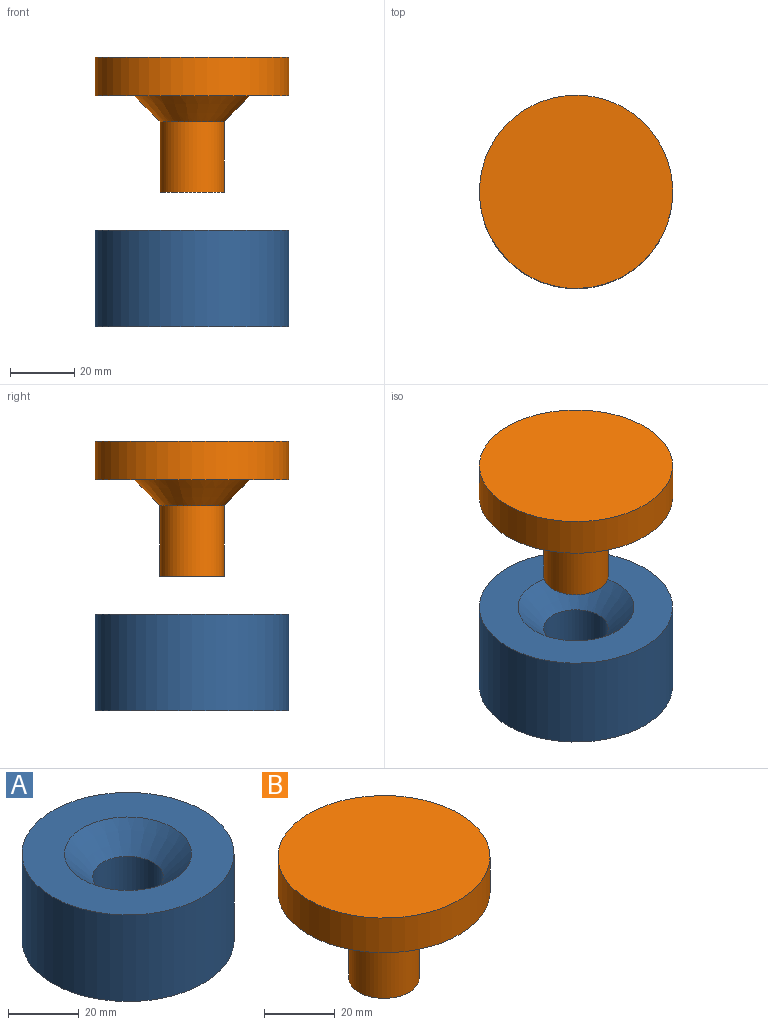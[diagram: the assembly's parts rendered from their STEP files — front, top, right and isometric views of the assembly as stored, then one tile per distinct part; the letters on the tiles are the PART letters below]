
ASSEMBLY  parts=2 mates=1
PART A: 5 faces, bbox 60x60x30 mm
  f0: plane 60x60mm, normal (0,0,-1), area 2513.3mm2, adj f1,f4
  f1: cylinder r=10mm len=22mm, axis (0,0,-1), area 1382.3mm2, adj f0,f2
  f2: cone r=10mm half-angle=45deg, axis (0,0,1), area 995.2mm2, adj f1,f3
  f3: plane 60x60mm, normal (0,0,1), area 1809.6mm2, adj f2,f4
  f4: cylinder r=30mm len=60mm, axis (0,0,-1), area 5654.9mm2, adj f0,f3
PART B: 6 faces, bbox 60x60x42 mm
  f0: plane 60x60mm, normal (0,0,1), area 2827.4mm2, adj f1
  f1: cylinder r=30mm len=60mm, axis (0,0,-1), area 2261.9mm2, adj f0,f2
  f2: plane 60x60mm, normal (0,0,-1), area 1809.6mm2, adj f1,f3
  f3: cone r=9.95mm half-angle=45deg, axis (0,0,1), area 999.6mm2, adj f2,f4
  f4: cylinder r=9.95mm len=21.95mm, axis (0,0,-1), area 1372.3mm2, adj f3,f5
  f5: plane 19.9x19.9mm, normal (0,0,-1), area 311mm2, adj f4
PLACE A t=(-0.84,-7.45,-4.56)mm
PLACE B t=(-0.84,-7.45,37.23)mm
MATE cylindrical B.f1 <-> A.f1  axis (0,0,-1) through (-0.84,-7.45,48.21)mm
